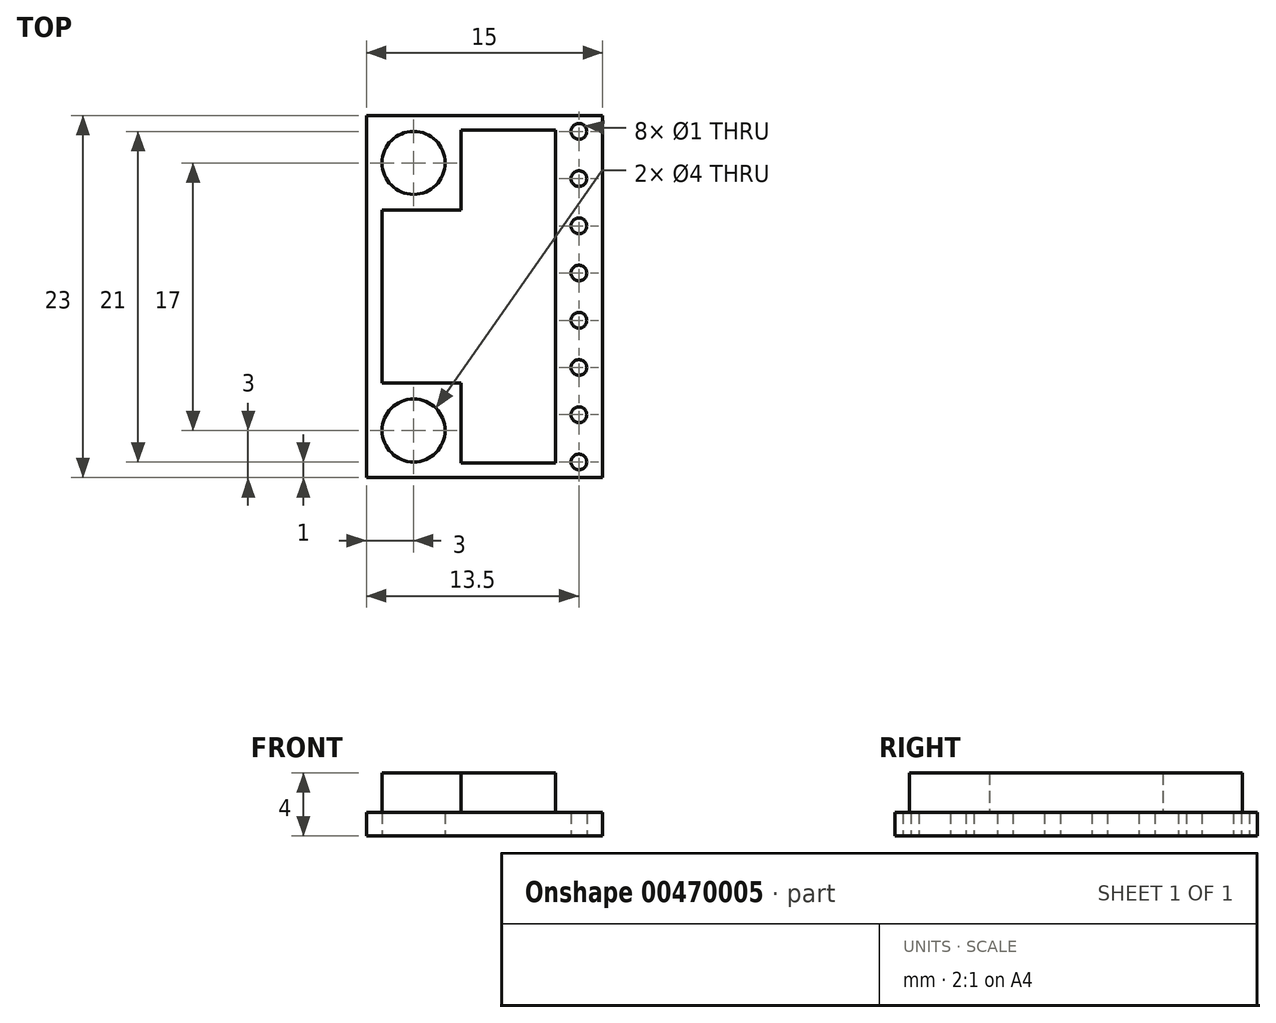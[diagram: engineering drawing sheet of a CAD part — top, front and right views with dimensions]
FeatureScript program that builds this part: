
annotation { "Feature Type Name" : "Feature", "Feature Type Description" : "" }
export const myFeature = defineFeature(function(context is Context, id is Id, definition is map)
    precondition{}
    {
        {
            var Q0;
            Q0=qCreatedBy(makeId("Top.planeOp"),FACE);
            var sketch = newSketch(context, id + "F0", { "sketchPlane" : qUnion([Q0])});
            skLineSegment(sketch, "E0.bottom", {"start": v(7.5, -11.5) * mm, "end": v(-7.5, -11.5) * mm});
            skLineSegment(sketch, "E0.top", {"start": v(7.5, 11.5) * mm, "end": v(-7.5, 11.5) * mm});
            skLineSegment(sketch, "E0.left", {"start": v(7.5, -11.5) * mm, "end": v(7.5, 11.5) * mm});
            skLineSegment(sketch, "E0.right", {"start": v(-7.5, -11.5) * mm, "end": v(-7.5, 11.5) * mm});
            skPoint(sketch, "E0.middle", {"position": v(0, 0) * mm});
            skCircle(sketch, "E1", {"center": v(-4.5, 8.5) * mm, "radius": 2 * mm});
            skCircle(sketch, "E2", {"center": v(-4.5, -8.5) * mm, "radius": 2 * mm});
            skCircle(sketch, "E3", {"center": v(6, 10.5) * mm, "radius": 0.5 * mm});
            skCircle(sketch, "E4.1.0.0", {"center": v(6, 7.5) * mm, "radius": 0.5 * mm});
            skCircle(sketch, "E4.2.0.0", {"center": v(6, 4.5) * mm, "radius": 0.5 * mm});
            skLineSegment(sketch, "E4.direction1", {"start": v(6, 10.5) * mm, "end": v(6, 7.5) * mm, "construction": true});
            skCircle(sketch, "E5", {"center": v(6, 1.5) * mm, "radius": 0.5 * mm});
            skCircle(sketch, "E6.MirrorC", {"center": v(6, -4.5) * mm, "radius": 0.5 * mm});
            skCircle(sketch, "E7.MirrorC", {"center": v(6, -1.5) * mm, "radius": 0.5 * mm});
            skCircle(sketch, "E8.MirrorC", {"center": v(6, -7.5) * mm, "radius": 0.5 * mm});
            skCircle(sketch, "E9.MirrorC", {"center": v(6, -10.5) * mm, "radius": 0.5 * mm});
            skLineSegment(sketch, "E10.bottom", {"start": v(4.5, -10.57) * mm, "end": v(-1.5, -10.57) * mm});
            skLineSegment(sketch, "E10.top", {"start": v(4.5, 10.57) * mm, "end": v(-1.5, 10.57) * mm});
            skLineSegment(sketch, "E10.left", {"start": v(4.5, -10.57) * mm, "end": v(4.5, 10.57) * mm});
            skLineSegment(sketch, "E10.right", {"start": v(-1.5, -10.57) * mm, "end": v(-1.5, 10.57) * mm});
            skPoint(sketch, "E10.middle", {"position": v(1.5, 0) * mm});
            skLineSegment(sketch, "E11.bottom", {"start": v(-1.5, 5.5) * mm, "end": v(-6.5, 5.5) * mm});
            skLineSegment(sketch, "E11.top", {"start": v(-1.5, -5.5) * mm, "end": v(-6.5, -5.5) * mm});
            skLineSegment(sketch, "E11.left", {"start": v(-1.5, 5.5) * mm, "end": v(-1.5, -5.5) * mm});
            skLineSegment(sketch, "E11.right", {"start": v(-6.5, 5.5) * mm, "end": v(-6.5, -5.5) * mm});
            skSolve(sketch);
        }
        {
            var Q0;
            {var subQ4=sQuery(id+"F0.wireOp",EDGE,"E10.bottom");Q0=makeQuery(id+"F0.imprint","IMPRINT",FACE,{"disambiguationData":[TD([[makeQuery(id+"F0.imprint","IMPRINT",EDGE,{"derivedFrom":subQ4}),-1.0]])]});}
            var Q1;
            {var subQ2=sQuery(id+"F0.wireOp",EDGE,"E11.bottom");Q1=makeQuery(id+"F0.imprint","IMPRINT",FACE,{"disambiguationData":[TD([[makeQuery(id+"F0.imprint","IMPRINT",EDGE,{"derivedFrom":subQ2}),1.0]])]});}
            extrude(context, id + "F1", {"entities" : qUnion([Q0, Q1]), "depth" : 4 * mm, "offsetDistance" : 25 * mm});
        }
        {
            var Q0;
            Q0=makeQuery(id+"F0.imprint","IMPRINT",FACE,{"disambiguationData":[TD([[makeQuery(id+"F0.imprint","IMPRINT",EDGE,{"derivedFrom":sQuery(id+"F0.wireOp",EDGE,"E0.bottom")}),-1.0]])]});
            extrude(context, id + "F2", {"entities" : qUnion([Q0]), "operationType" : NewBodyOperationType.ADD, "depth" : 1.5 * mm, "offsetDistance" : 25 * mm});
        }
    });
